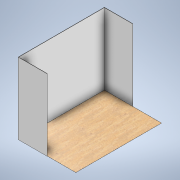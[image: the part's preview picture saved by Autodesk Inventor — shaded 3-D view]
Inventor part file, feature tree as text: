
AUTODESK INVENTOR PART (.ipt)
format: ipt  version: 2020 (Build 240168000, 168)  size: 138,752 bytes
history: native  units: in
note: dims shown in document units (in); Inventor stores cm internally (conversion verified against a paired STEP export)
features: extrude x2, sketch x2
ambient origin geometry x8: Origin, YZ Plane, XZ Plane, XY Plane, X Axis, Y Axis, Z Axis, Center Point
bodies: Body1 (feature_tree)
feature tree (4):
  extrude  "Extrusion2"  Depth=118.1102in
  extrude  "Extrusion3"  Depth=0.3937in
  sketch  "Sketch1"  dims[d2=78.7402in d3=118.1102in]
  sketch  "Sketch3"  dims[d4=0.0394in d5=0.0in d6=0.3937in d7=0.3937in d8=39.3701in d9=39.3701in d10=0.3937in d11=98.4252in d12=0.0in]
